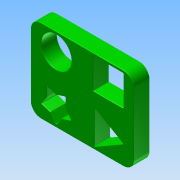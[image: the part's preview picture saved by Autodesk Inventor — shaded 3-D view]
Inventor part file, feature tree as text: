
AUTODESK INVENTOR PART (.ipt)
format: ipt  version: 2014 (Build 180170000, 170)  size: 258,048 bytes
history: native  units: in
note: dims shown in document units (in); Inventor stores cm internally (conversion verified against a paired STEP export)
features: extrude x1, fillet x1, shell x1, sketch x1
ambient origin geometry x8: Origin, YZ Plane, XZ Plane, XY Plane, X Axis, Y Axis, Z Axis, Center Point
bodies: Solid1 (feature_tree)
feature tree (4):
  extrude  "Extrusion1"  Depth=1.59in
  fillet  "Fillet1"  Radius=0.2in
  shell  "Shell1"  Thickness=0.6051in
  sketch  "Sketch1"  dims[d0=1.975in d1=1.59in d2=0.2in d3=0.6051in d4=0.187in d5=0.58in d6=0.638in d7=0.58in d8=0.05in d9=0.05in d10=0.05in d11=0.05in d12=0.2in d13=0.2in d14=0.2in d15=0.2in d16=0.3in d17=0.0in d18=0.01in d19=0.01in]
